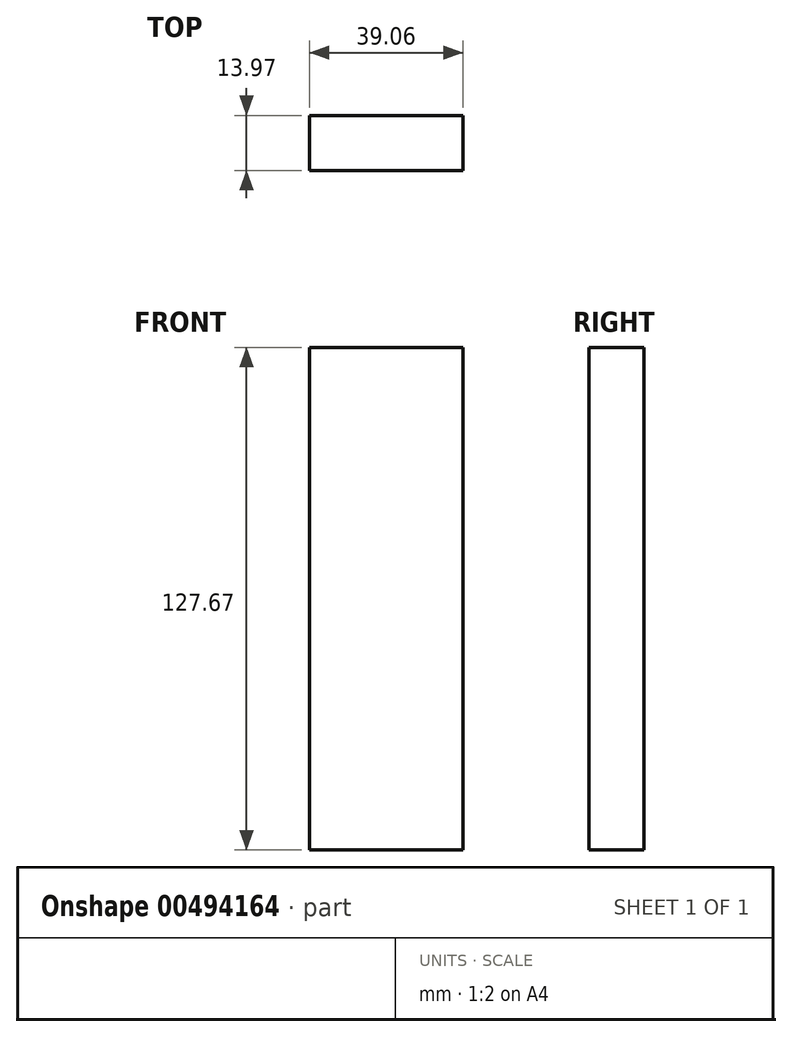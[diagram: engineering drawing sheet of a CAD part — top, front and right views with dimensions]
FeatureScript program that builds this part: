
annotation { "Feature Type Name" : "Feature", "Feature Type Description" : "" }
export const myFeature = defineFeature(function(context is Context, id is Id, definition is map)
    precondition{}
    {
        {
            var Q0;
            Q0=qCreatedBy(makeId("Front.planeOp"),FACE);
            var sketch = newSketch(context, id + "F0", { "sketchPlane" : qUnion([Q0])});
            skLineSegment(sketch, "E0.bottom", {"start": v(-19.53, 61.36) * mm, "end": v(19.53, 61.36) * mm});
            skLineSegment(sketch, "E0.top", {"start": v(-19.53, -66.31) * mm, "end": v(19.53, -66.31) * mm});
            skLineSegment(sketch, "E0.left", {"start": v(-19.53, 61.36) * mm, "end": v(-19.53, -66.31) * mm});
            skLineSegment(sketch, "E0.right", {"start": v(19.53, 61.36) * mm, "end": v(19.53, -66.31) * mm});
            skSolve(sketch);
        }
        {
            var Q0;
            Q0 = qSketchRegion(id + "F0", true);
            extrude(context, id + "F1", {"entities" : qUnion([Q0]), "depth" : 13.97 * mm});
        }
    });
